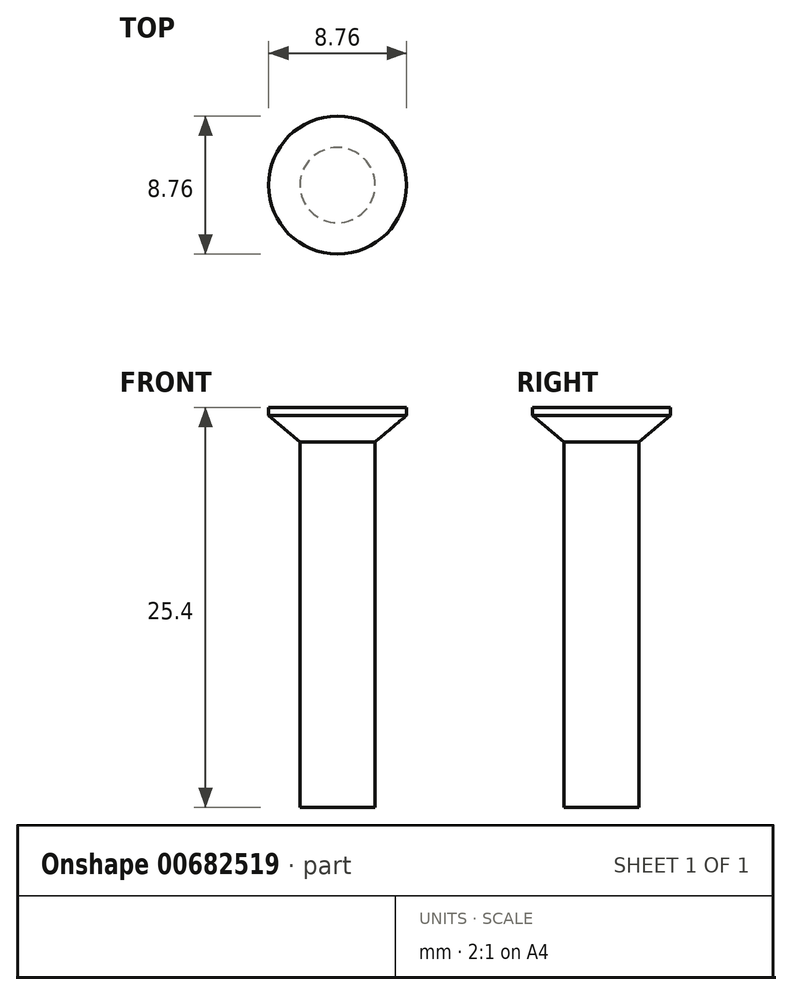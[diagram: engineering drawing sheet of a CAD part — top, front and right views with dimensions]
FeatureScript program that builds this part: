
annotation { "Feature Type Name" : "Feature", "Feature Type Description" : "" }
export const myFeature = defineFeature(function(context is Context, id is Id, definition is map)
    precondition{}
    {
        {
            var Q0;
            Q0=qCreatedBy(makeId("Front.planeOp"),FACE);
            var sketch = newSketch(context, id + "F0", { "sketchPlane" : qUnion([Q0])});
            skLineSegment(sketch, "E0", {"start": v(0, 0) * mm, "end": v(-4.38, 0) * mm});
            skLineSegment(sketch, "E1", {"start": v(-4.38, 0) * mm, "end": v(-4.38, -0.5) * mm});
            skLineSegment(sketch, "E2", {"start": v(-4.38, -0.5) * mm, "end": v(-2.39, -2.18) * mm});
            skLineSegment(sketch, "E3", {"start": v(-2.39, -2.18) * mm, "end": v(-2.39, -25.4) * mm});
            skLineSegment(sketch, "E4", {"start": v(-2.39, -25.4) * mm, "end": v(0, -25.4) * mm});
            skLineSegment(sketch, "E5", {"start": v(0, -25.4) * mm, "end": v(0, 0) * mm});
            skLineSegment(sketch, "E6", {"start": v(-4.38, -0.5) * mm, "end": v(0, -0.5) * mm, "construction": true});
            skLineSegment(sketch, "E7", {"start": v(-2.39, -2.18) * mm, "end": v(-2.39, -0.5) * mm, "construction": true});
            skLineSegment(sketch, "E8", {"start": v(0, 86.3) * mm, "end": v(0, -39.42) * mm, "construction": true});
            skSolve(sketch);
        }
        {
            var Q0;
            Q0 = qSketchRegion(id + "F0", true);
            var Q1;
            Q1=sQuery(id+"F0.wireOp",EDGE,"E8");
            revolve(context, id + "F1", {"entities" : qUnion([Q0]), "axis" : qUnion([Q1]), "revolveType" : RevolveType.FULL});
        }
    });
